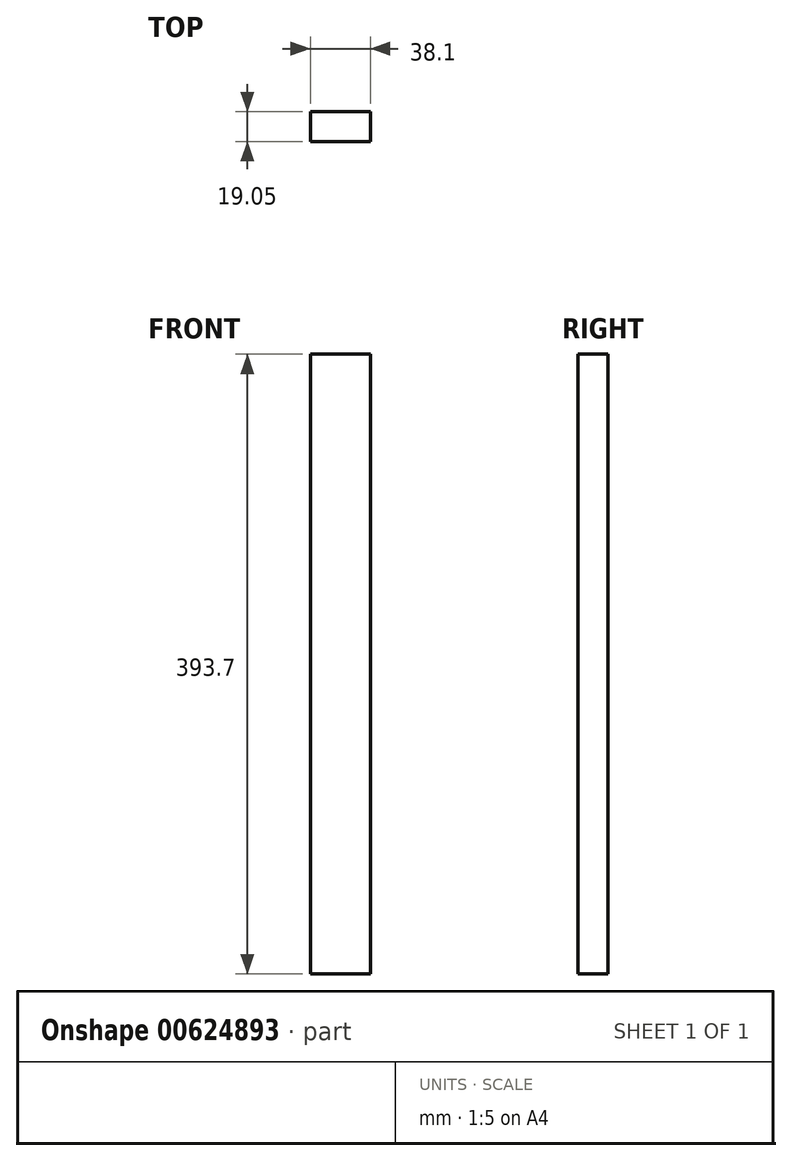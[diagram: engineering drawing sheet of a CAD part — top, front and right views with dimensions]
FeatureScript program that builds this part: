
annotation { "Feature Type Name" : "Feature", "Feature Type Description" : "" }
export const myFeature = defineFeature(function(context is Context, id is Id, definition is map)
    precondition{}
    {
        {
            var Q0;
            Q0=qCreatedBy(makeId("Top.planeOp"),FACE);
            var sketch = newSketch(context, id + "F0", { "sketchPlane" : qUnion([Q0])});
            skLineSegment(sketch, "E0.bottom", {"start": v(0, 0) * mm, "end": v(-38.1, 0) * mm});
            skLineSegment(sketch, "E0.top", {"start": v(0, 19.05) * mm, "end": v(-38.1, 19.05) * mm});
            skLineSegment(sketch, "E0.left", {"start": v(0, 0) * mm, "end": v(0, 19.05) * mm});
            skLineSegment(sketch, "E0.right", {"start": v(-38.1, 0) * mm, "end": v(-38.1, 19.05) * mm});
            skSolve(sketch);
        }
        {
            var Q0;
            Q0=makeQuery(id+"F0.imprint","IMPRINT",FACE,{"disambiguationData":[TD([[makeQuery(id+"F0.imprint","IMPRINT",EDGE,{"derivedFrom":sQuery(id+"F0.wireOp",EDGE,"E0.bottom")}),-1.0]])]});
            extrude(context, id + "F1", {"entities" : qUnion([Q0]), "oppositeDirection" : true, "depth" : 393.7 * mm, "offsetDistance" : 25.4 * mm});
        }
    });
